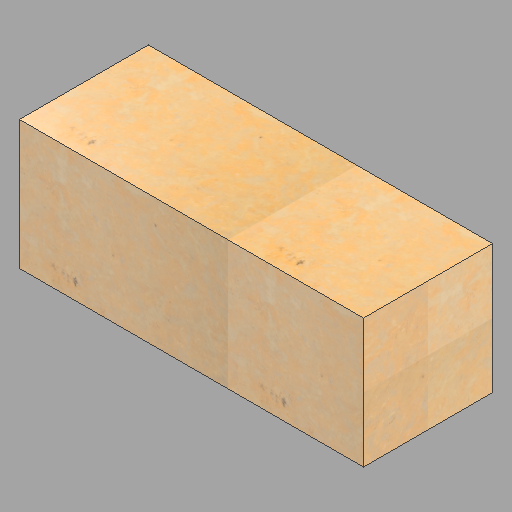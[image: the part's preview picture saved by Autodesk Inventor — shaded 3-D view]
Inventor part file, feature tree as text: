
AUTODESK INVENTOR PART (.ipt)
format: ipt  version: 2022.2 (Build 262287010, 287A)  size: 324,608 bytes
history: native  units: in
note: dims shown in document units (in); Inventor stores cm internally (conversion verified against a paired STEP export)
features: other x1, extrude x1, sketch x1
ambient origin geometry x8: Origin, YZ Plane, XZ Plane, XY Plane, X Axis, Y Axis, Z Axis, Center Point
bodies: Solid1 (feature_tree)
feature tree (3):
  other  "Bench - 34"
  extrude  "Extrusion1"  Depth=18.0in
  sketch  "Sketch1"  dims[d0=18.0in d1=18.0in d2=48.0in d3=0.0in]
